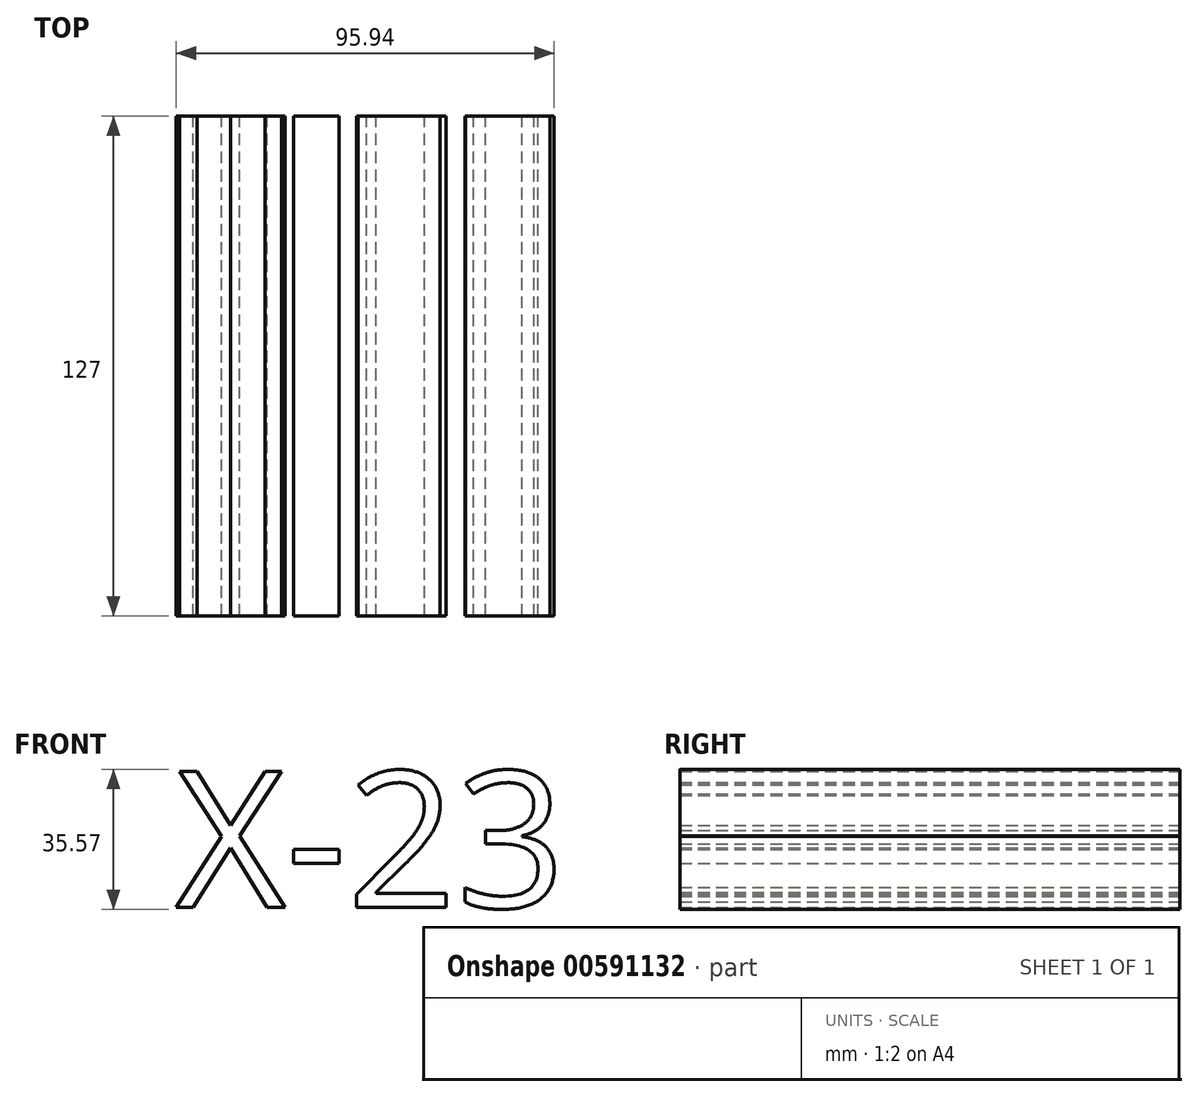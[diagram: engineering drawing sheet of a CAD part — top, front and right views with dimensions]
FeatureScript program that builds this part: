
annotation { "Feature Type Name" : "Feature", "Feature Type Description" : "" }
export const myFeature = defineFeature(function(context is Context, id is Id, definition is map)
    precondition{}
    {
        {
            var Q0;
            Q0=qCreatedBy(makeId("Front.planeOp"),FACE);
            var sketch = newSketch(context, id + "F0", { "sketchPlane" : qUnion([Q0])});
            skText(sketch, "E0", { "text": "X-23\n", "fontName": "OpenSans-Regular.ttf"});
            const initialGuessF0  = {"E0": [-0.03574, 0.00939, 1, 0, 0.03489]};
            skSetInitialGuess(sketch, initialGuessF0);
            skSolve(sketch);
        }
        {
            var Q0;
            Q0 = qSketchRegion(id + "F0", true);
            extrude(context, id + "F1", {"entities" : qUnion([Q0]), "depth" : 127 * mm, "offsetDistance" : 25.4 * mm});
        }
    });
